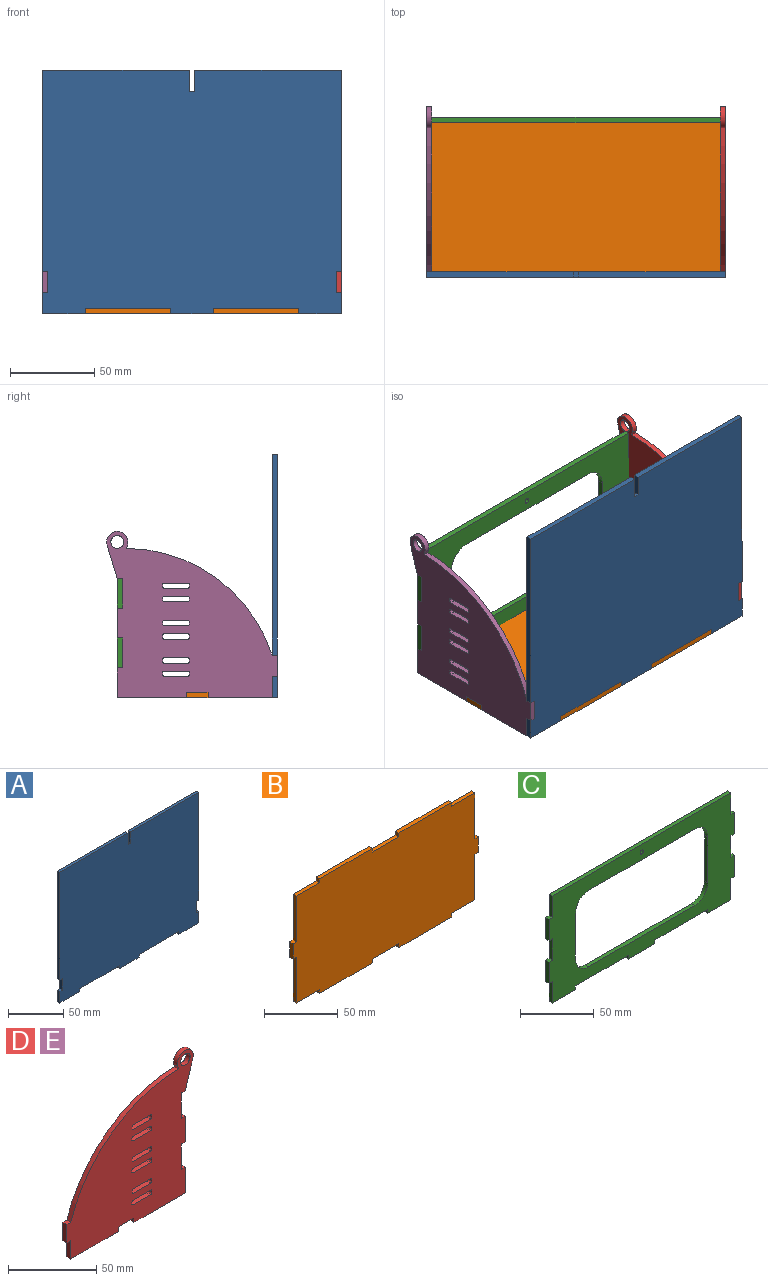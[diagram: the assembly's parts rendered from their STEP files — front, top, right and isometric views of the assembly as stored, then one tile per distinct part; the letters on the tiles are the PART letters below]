
ASSEMBLY  parts=5 mates=4
PART A: 26 faces, bbox 177.8x3.2x144.9 mm
  f0: plane 12.7x3.18mm, normal (1,0,0), area 40.3mm2, adj f1,f23,f24,f25
  f1: plane 87.31x3.18mm, normal (0,0,1), area 277.2mm2, adj f0,f2,f24,f25
  f2: plane 119.5x3.18mm, normal (-1,0,0), area 379.4mm2, adj f1,f3,f24,f25
  f3: plane 3.18x3.18mm, normal (0,0,-1), area 10.1mm2, adj f2,f4,f24,f25
  f4: plane 12.7x3.18mm, normal (-1,0,0), area 40.3mm2, adj f3,f5,f24,f25
  f5: plane 3.18x3.18mm, normal (0,0,1), area 10.1mm2, adj f4,f6,f24,f25
  f6: plane 12.7x3.18mm, normal (-1,0,0), area 40.3mm2, adj f5,f7,f24,f25
  f7: plane 25.4x3.18mm, normal (0,0,-1), area 80.6mm2, adj f6,f8,f24,f25
  f8: plane 3.18x3.18mm, normal (1,0,0), area 10.1mm2, adj f7,f9,f24,f25
  f9: plane 50.8x3.18mm, normal (0,0,-1), area 161.3mm2, adj f8,f10,f24,f25
  f10: plane 3.18x3.18mm, normal (-1,0,0), area 10.1mm2, adj f9,f11,f24,f25
  f11: plane 25.4x3.18mm, normal (0,0,-1), area 80.6mm2, adj f10,f12,f24,f25
  f12: plane 3.18x3.18mm, normal (1,0,0), area 10.1mm2, adj f11,f13,f24,f25
  f13: plane 50.8x3.18mm, normal (0,0,-1), area 161.3mm2, adj f12,f14,f24,f25
  f14: plane 3.18x3.18mm, normal (-1,0,0), area 10.1mm2, adj f13,f15,f24,f25
  f15: plane 25.4x3.18mm, normal (0,0,-1), area 80.6mm2, adj f14,f16,f24,f25
  f16: plane 12.7x3.18mm, normal (1,0,0), area 40.3mm2, adj f15,f17,f24,f25
  f17: plane 3.18x3.18mm, normal (0,0,1), area 10.1mm2, adj f16,f18,f24,f25
  f18: plane 12.7x3.18mm, normal (1,0,0), area 40.3mm2, adj f17,f19,f24,f25
  f19: plane 3.18x3.18mm, normal (0,0,-1), area 10.1mm2, adj f18,f20,f24,f25
  f20: plane 119.5x3.18mm, normal (1,0,0), area 379.4mm2, adj f19,f21,f24,f25
  f21: plane 87.31x3.18mm, normal (0,0,1), area 277.2mm2, adj f20,f22,f24,f25
  f22: plane 12.7x3.18mm, normal (-1,0,0), area 40.3mm2, adj f21,f23,f24,f25
  f23: plane 3.18x3.18mm, normal (0,0,1), area 10.1mm2, adj f0,f22,f24,f25
  f24: plane 177.8x144.9mm, normal (0,-1,0), area 25319.7mm2, adj f0,f1,f2,f3,f4,f5,f6,f7
  f25: plane 177.8x144.9mm, normal (0,1,0), area 25319.7mm2, adj f0,f1,f2,f3,f4,f5,f6,f7
PART B: 30 faces, bbox 177.8x3.2x95.3 mm
  f0: plane 50.8x3.18mm, normal (0,0,1), area 161.3mm2, adj f1,f27,f28,f29
  f1: plane 3.18x3.18mm, normal (-1,0,0), area 10.1mm2, adj f0,f2,f28,f29
  f2: plane 22.23x3.18mm, normal (0,0,1), area 70.6mm2, adj f1,f3,f28,f29
  f3: plane 38.1x3.18mm, normal (-1,0,0), area 121mm2, adj f2,f4,f28,f29
  f4: plane 3.18x3.18mm, normal (0,0,1), area 10.1mm2, adj f3,f5,f28,f29
  f5: plane 12.7x3.18mm, normal (-1,0,0), area 40.3mm2, adj f4,f6,f28,f29
  f6: plane 3.18x3.18mm, normal (0,0,-1), area 10.1mm2, adj f5,f7,f28,f29
  f7: plane 38.1x3.18mm, normal (-1,0,0), area 121mm2, adj f6,f8,f28,f29
  f8: plane 22.23x3.18mm, normal (0,0,-1), area 70.6mm2, adj f7,f9,f28,f29
  f9: plane 3.18x3.18mm, normal (-1,0,0), area 10.1mm2, adj f8,f10,f28,f29
  f10: plane 50.8x3.18mm, normal (0,0,-1), area 161.3mm2, adj f9,f11,f28,f29
  f11: plane 3.18x3.18mm, normal (1,0,0), area 10.1mm2, adj f10,f12,f28,f29
  f12: plane 25.4x3.18mm, normal (0,0,-1), area 80.6mm2, adj f11,f13,f28,f29
  f13: plane 3.18x3.18mm, normal (-1,0,0), area 10.1mm2, adj f12,f14,f28,f29
  f14: plane 50.8x3.18mm, normal (0,0,-1), area 161.3mm2, adj f13,f15,f28,f29
  f15: plane 3.18x3.18mm, normal (1,0,0), area 10.1mm2, adj f14,f16,f28,f29
  f16: plane 22.23x3.18mm, normal (0,0,-1), area 70.6mm2, adj f15,f17,f28,f29
  f17: plane 38.1x3.18mm, normal (1,0,0), area 121mm2, adj f16,f18,f28,f29
  f18: plane 3.18x3.18mm, normal (0,0,-1), area 10.1mm2, adj f17,f19,f28,f29
  f19: plane 12.7x3.18mm, normal (1,0,0), area 40.3mm2, adj f18,f20,f28,f29
  f20: plane 3.18x3.18mm, normal (0,0,1), area 10.1mm2, adj f19,f21,f28,f29
  f21: plane 38.1x3.18mm, normal (1,0,0), area 121mm2, adj f20,f22,f28,f29
  f22: plane 22.23x3.18mm, normal (0,0,1), area 70.6mm2, adj f21,f23,f28,f29
  f23: plane 3.18x3.18mm, normal (1,0,0), area 10.1mm2, adj f22,f24,f28,f29
  f24: plane 50.8x3.18mm, normal (0,0,1), area 161.3mm2, adj f23,f25,f28,f29
  f25: plane 3.18x3.18mm, normal (-1,0,0), area 10.1mm2, adj f24,f26,f28,f29
  f26: plane 25.4x3.18mm, normal (0,0,1), area 80.6mm2, adj f25,f27,f28,f29
  f27: plane 3.18x3.18mm, normal (1,0,0), area 10.1mm2, adj f0,f26,f28,f29
  f28: plane 177.8x95.25mm, normal (0,-1,0), area 15967.7mm2, adj f0,f1,f2,f3,f4,f5,f6,f7
  f29: plane 177.8x95.25mm, normal (0,1,0), area 15967.7mm2, adj f0,f1,f2,f3,f4,f5,f6,f7
PART C: 39 faces, bbox 177.8x3.2x88.9 mm
  f0: cylinder r=12.7mm len=12.7mm, axis (0,1,0), area 63.3mm2, adj f1,f34,f37,f38
  f1: plane 38.1x3.18mm, normal (-1,0,0), area 121mm2, adj f0,f2,f37,f38
  f2: cylinder r=12.7mm len=12.7mm, axis (0,1,0), area 63.3mm2, adj f1,f3,f37,f38
  f3: plane 101.6x3.18mm, normal (0,0,1), area 322.6mm2, adj f2,f4,f37,f38
  f4: cylinder r=12.7mm len=12.7mm, axis (0,1,0), area 63.3mm2, adj f3,f5,f37,f38
  f5: plane 38.1x3.18mm, normal (1,0,0), area 121mm2, adj f4,f6,f37,f38
  f6: cylinder r=12.7mm len=12.7mm, axis (0,1,0), area 63.3mm2, adj f5,f34,f37,f38
  f7: plane 171.45x3.18mm, normal (0,0,1), area 544.4mm2, adj f8,f35,f37,f38
  f8: plane 17.78x3.18mm, normal (-1,0,0), area 56.5mm2, adj f7,f9,f37,f38
  f9: plane 3.18x3.18mm, normal (0,0,1), area 10.1mm2, adj f8,f10,f37,f38
  f10: plane 17.78x3.18mm, normal (-1,0,0), area 56.5mm2, adj f9,f11,f37,f38
  f11: plane 3.18x3.18mm, normal (0,0,-1), area 10.1mm2, adj f10,f12,f37,f38
  f12: plane 17.78x3.18mm, normal (-1,0,0), area 56.5mm2, adj f11,f13,f37,f38
  f13: plane 3.18x3.18mm, normal (0,0,1), area 10.1mm2, adj f12,f14,f37,f38
  f14: plane 17.78x3.18mm, normal (-1,0,0), area 56.5mm2, adj f13,f15,f37,f38
  f15: plane 3.18x3.18mm, normal (0,0,-1), area 10.1mm2, adj f14,f16,f37,f38
  f16: plane 17.78x3.18mm, normal (-1,0,0), area 56.5mm2, adj f15,f17,f37,f38
  f17: plane 22.23x3.18mm, normal (0,0,-1), area 70.6mm2, adj f16,f18,f37,f38
  f18: plane 3.18x3.18mm, normal (1,0,0), area 10.1mm2, adj f17,f19,f37,f38
  f19: plane 50.8x3.18mm, normal (0,0,-1), area 161.3mm2, adj f18,f20,f37,f38
  f20: plane 3.18x3.18mm, normal (-1,0,0), area 10.1mm2, adj f19,f21,f37,f38
  f21: plane 25.4x3.18mm, normal (0,0,-1), area 80.6mm2, adj f20,f22,f37,f38
  f22: plane 3.18x3.18mm, normal (1,0,0), area 10.1mm2, adj f21,f23,f37,f38
  f23: plane 50.8x3.18mm, normal (0,0,-1), area 161.3mm2, adj f22,f24,f37,f38
  f24: plane 3.18x3.18mm, normal (-1,0,0), area 10.1mm2, adj f23,f25,f37,f38
  f25: plane 22.23x3.18mm, normal (0,0,-1), area 70.6mm2, adj f24,f26,f37,f38
  f26: plane 17.78x3.18mm, normal (1,0,0), area 56.5mm2, adj f25,f27,f37,f38
  f27: plane 3.18x3.18mm, normal (0,0,-1), area 10.1mm2, adj f26,f28,f37,f38
  f28: plane 17.78x3.18mm, normal (1,0,0), area 56.5mm2, adj f27,f29,f37,f38
  f29: plane 3.18x3.18mm, normal (0,0,1), area 10.1mm2, adj f28,f30,f37,f38
  f30: plane 17.78x3.18mm, normal (1,0,0), area 56.5mm2, adj f29,f31,f37,f38
  f31: plane 3.18x3.18mm, normal (0,0,-1), area 10.1mm2, adj f30,f32,f37,f38
  f32: plane 17.78x3.18mm, normal (1,0,0), area 56.5mm2, adj f31,f33,f37,f38
  f33: plane 3.18x3.18mm, normal (0,0,1), area 10.1mm2, adj f32,f35,f37,f38
  f34: plane 101.6x3.18mm, normal (0,0,-1), area 322.6mm2, adj f0,f6,f37,f38
  f35: plane 17.78x3.18mm, normal (1,0,0), area 56.5mm2, adj f7,f33,f37,f38
  f36: cylinder r=1.59mm len=3.18mm, axis (0,1,0), area 31.7mm2, adj f37,f38
  f37: plane 177.8x88.9mm, normal (0,-1,0), area 7211.2mm2, adj f0,f1,f2,f3,f4,f5,f6,f7
  f38: plane 177.8x88.9mm, normal (0,1,0), area 7211.2mm2, adj f0,f1,f2,f3,f4,f5,f6,f7
PART D: 72 faces, bbox 101.6x3.2x99.1 mm
  f0: cylinder r=91.78mm len=86.6mm, axis (0,1,0), area 364.2mm2, adj f14,f66,f67,f68
  f1: plane 38.1x3.18mm, normal (0,0,-1), area 121mm2, adj f2,f65,f66,f67
  f2: plane 3.18x3.18mm, normal (1,0,0), area 10.1mm2, adj f1,f3,f66,f67
  f3: plane 12.7x3.18mm, normal (0,0,-1), area 40.3mm2, adj f2,f4,f66,f67
  f4: plane 3.18x3.18mm, normal (-1,0,0), area 10.1mm2, adj f3,f5,f66,f67
  f5: plane 41.28x3.18mm, normal (0,0,-1), area 131mm2, adj f4,f6,f66,f67
  f6: plane 17.78x3.18mm, normal (1,0,0), area 56.5mm2, adj f5,f7,f66,f67
  f7: plane 3.18x3.18mm, normal (0,0,1), area 10.1mm2, adj f6,f8,f66,f67
  f8: plane 17.78x3.18mm, normal (1,0,0), area 56.5mm2, adj f7,f9,f66,f67
  f9: plane 3.18x3.18mm, normal (0,0,-1), area 10.1mm2, adj f8,f10,f66,f67
  f10: plane 17.78x3.18mm, normal (1,0,0), area 56.5mm2, adj f9,f11,f66,f67
  f11: plane 3.18x3.18mm, normal (0,0,1), area 10.1mm2, adj f10,f12,f66,f67
  f12: plane 17.78x3.18mm, normal (1,0,0), area 56.5mm2, adj f11,f13,f66,f67
  f13: plane 3.18x3.18mm, normal (0,0,-1), area 10.1mm2, adj f12,f66,f67,f69
  f14: plane 3.18x3.18mm, normal (0,0,1), area 10.1mm2, adj f0,f15,f66,f67
  f15: plane 12.7x3.18mm, normal (-1,0,0), area 40.3mm2, adj f14,f16,f66,f67
  f16: plane 3.18x3.18mm, normal (0,0,-1), area 10.1mm2, adj f15,f65,f66,f67
  f17: cylinder r=1mm len=3.18mm, axis (0,1,0), area 5mm2, adj f18,f59,f66,f67
  f18: plane 13.88x3.18mm, normal (0,0,-1), area 44.1mm2, adj f17,f19,f66,f67
  f19: cylinder r=1mm len=3.18mm, axis (0,1,0), area 5mm2, adj f18,f20,f66,f67
  f20: plane 3.18x1.18mm, normal (-1,0,0), area 3.7mm2, adj f19,f21,f66,f67
  f21: cylinder r=1mm len=3.18mm, axis (0,1,0), area 5mm2, adj f20,f22,f66,f67
  f22: plane 13.88x3.18mm, normal (0,0,1), area 44.1mm2, adj f21,f23,f66,f67
  f23: cylinder r=1mm len=3.18mm, axis (0,1,0), area 5mm2, adj f22,f59,f66,f67
  f24: cylinder r=1mm len=3.18mm, axis (0,1,0), area 5mm2, adj f25,f60,f66,f67
  f25: plane 13.88x3.18mm, normal (0,0,-1), area 44.1mm2, adj f24,f26,f66,f67
  f26: cylinder r=1mm len=3.18mm, axis (0,1,0), area 5mm2, adj f25,f27,f66,f67
  f27: plane 3.18x1.18mm, normal (-1,0,0), area 3.7mm2, adj f26,f28,f66,f67
  f28: cylinder r=1mm len=3.18mm, axis (0,1,0), area 5mm2, adj f27,f29,f66,f67
  f29: plane 13.88x3.18mm, normal (0,0,1), area 44.1mm2, adj f28,f30,f66,f67
  f30: cylinder r=1mm len=3.18mm, axis (0,1,0), area 5mm2, adj f29,f60,f66,f67
  f31: cylinder r=1mm len=3.18mm, axis (0,1,0), area 5mm2, adj f32,f61,f66,f67
  f32: plane 3.18x1.18mm, normal (1,0,0), area 3.7mm2, adj f31,f33,f66,f67
  f33: cylinder r=1mm len=3.18mm, axis (0,1,0), area 5mm2, adj f32,f34,f66,f67
  f34: plane 13.88x3.18mm, normal (0,0,-1), area 44.1mm2, adj f33,f35,f66,f67
  f35: cylinder r=1mm len=3.18mm, axis (0,1,0), area 5mm2, adj f34,f36,f66,f67
  f36: plane 3.18x1.18mm, normal (-1,0,0), area 3.7mm2, adj f35,f37,f66,f67
  f37: cylinder r=1mm len=3.18mm, axis (0,1,0), area 5mm2, adj f36,f61,f66,f67
  f38: cylinder r=1mm len=3.18mm, axis (0,1,0), area 5mm2, adj f39,f62,f66,f67
  f39: plane 3.18x1.18mm, normal (1,0,0), area 3.7mm2, adj f38,f40,f66,f67
  f40: cylinder r=1mm len=3.18mm, axis (0,1,0), area 5mm2, adj f39,f41,f66,f67
  f41: plane 13.88x3.18mm, normal (0,0,-1), area 44.1mm2, adj f40,f42,f66,f67
  f42: cylinder r=1mm len=3.18mm, axis (0,1,0), area 5mm2, adj f41,f43,f66,f67
  f43: plane 3.18x1.18mm, normal (-1,0,0), area 3.7mm2, adj f42,f44,f66,f67
  f44: cylinder r=1mm len=3.18mm, axis (0,1,0), area 5mm2, adj f43,f62,f66,f67
  f45: cylinder r=1mm len=3.18mm, axis (0,1,0), area 5mm2, adj f46,f63,f66,f67
  f46: plane 3.18x1.18mm, normal (1,0,0), area 3.7mm2, adj f45,f47,f66,f67
  f47: cylinder r=1mm len=3.18mm, axis (0,1,0), area 5mm2, adj f46,f48,f66,f67
  f48: plane 13.88x3.18mm, normal (0,0,-1), area 44.1mm2, adj f47,f49,f66,f67
  f49: cylinder r=1mm len=3.18mm, axis (0,1,0), area 5mm2, adj f48,f50,f66,f67
  f50: plane 3.18x1.18mm, normal (-1,0,0), area 3.7mm2, adj f49,f51,f66,f67
  f51: cylinder r=1mm len=3.18mm, axis (0,1,0), area 5mm2, adj f50,f63,f66,f67
  f52: cylinder r=1mm len=3.18mm, axis (0,1,0), area 5mm2, adj f53,f64,f66,f67
  f53: plane 13.88x3.18mm, normal (0,0,-1), area 44.1mm2, adj f52,f54,f66,f67
  f54: cylinder r=1mm len=3.18mm, axis (0,1,0), area 5mm2, adj f53,f55,f66,f67
  f55: plane 3.18x1.18mm, normal (-1,0,0), area 3.7mm2, adj f54,f56,f66,f67
  f56: cylinder r=1mm len=3.18mm, axis (0,1,0), area 5mm2, adj f55,f57,f66,f67
  f57: plane 13.88x3.18mm, normal (0,0,1), area 44.1mm2, adj f56,f58,f66,f67
  f58: cylinder r=1mm len=3.18mm, axis (0,1,0), area 5mm2, adj f57,f64,f66,f67
  f59: plane 3.18x1.18mm, normal (1,0,0), area 3.7mm2, adj f17,f23,f66,f67
  f60: plane 3.18x1.18mm, normal (1,0,0), area 3.7mm2, adj f24,f30,f66,f67
  f61: plane 13.88x3.18mm, normal (0,0,1), area 44.1mm2, adj f31,f37,f66,f67
  f62: plane 13.88x3.18mm, normal (0,0,1), area 44.1mm2, adj f38,f44,f66,f67
  f63: plane 13.88x3.18mm, normal (0,0,1), area 44.1mm2, adj f45,f51,f66,f67
  f64: plane 3.18x1.18mm, normal (1,0,0), area 3.7mm2, adj f52,f58,f66,f67
  f65: plane 12.7x3.18mm, normal (-1,0,0), area 40.3mm2, adj f1,f16,f66,f67
  f66: plane 101.6x99.06mm, normal (0,-1,0), area 6405mm2, adj f0,f1,f2,f3,f4,f5,f6,f7
  f67: plane 101.6x99.06mm, normal (0,1,0), area 6405mm2, adj f0,f1,f2,f3,f4,f5,f6,f7
  f68: plane 3.18x1.95mm, normal (-0.96,0,-0.29), area 6.5mm2, adj f0,f66,f67,f71
  f69: plane 19.72x6.07mm, normal (0.96,0,-0.29), area 65.5mm2, adj f13,f66,f67,f71
  f70: cylinder r=3.81mm len=7.62mm, axis (0,-1,0), area 76mm2, adj f66,f67
  f71: cylinder r=6.35mm len=12.7mm, axis (0,-1,0), area 75.4mm2, adj f66,f67,f68,f69
PART E: same geometry as D
PLACE A t=(0,-92.08,62.35)mm
PLACE B rot(axis=(-1,0,0),90deg) t=(0,-47.63,-82.55)mm
PLACE C t=(0,0,6.35)mm
PLACE D rot(axis=(0,0,1),90deg) t=(85.72,-49.21,-82.55)mm
PLACE E rot(axis=(0,0,1),90deg) t=(-88.9,-49.21,-82.55)mm
MATE revolute D.f65 <-> A.f25  axis (0,-1,0) through (88.9,-92.08,-82.55)mm
MATE revolute E.f65 <-> A.f25  axis (0,-1,0) through (-88.9,-92.08,-82.55)mm
MATE revolute C.f32 <-> D.f66  axis (1,0,0) through (88.9,0,-29.21)mm
MATE fastened B.f28 <-> E.f3  axis (0,0,1) through (-88.9,-47.63,-79.38)mm
